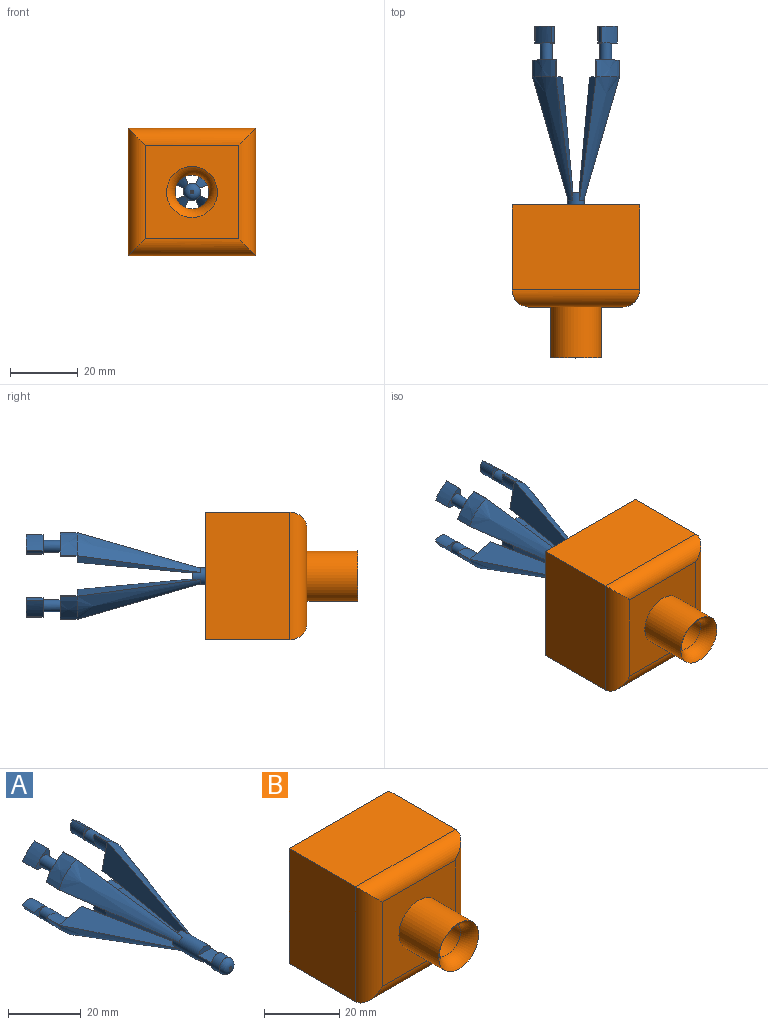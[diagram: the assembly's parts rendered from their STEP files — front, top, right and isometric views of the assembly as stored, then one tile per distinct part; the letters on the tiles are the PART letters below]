
ASSEMBLY  parts=2 mates=1
PART A: 81 faces, bbox 25.6x69x25.6 mm
  f0: plane 4.85x1.9mm, normal (0,-1,0), area 6.8mm2, adj f69,f74
  f1: bspline ~36.31x11.75mm, area 221.5mm2, adj f2,f3,f9,f69
  f2: bspline ~36.31x12.1mm, area 190.1mm2, adj f1,f3,f5,f6,f69,f71
  f3: bspline ~36.27x12.11mm, area 190.1mm2, adj f1,f2,f5,f8,f69,f71
  f4: plane 5.32x4.19mm, normal (0,1,0), area 7mm2, adj f7,f8,f9,f11
  f5: plane 8.66x8.66mm, normal (0,1,0), area 18.3mm2, adj f2,f3,f7
  f6: plane 5x0.12mm, normal (0.98,0,0.22), area 0.6mm2, adj f2,f7,f9,f10
  f7: cylinder r=5.66mm len=6.84mm, axis (0,-1,0), area 56.3mm2, adj f4,f5,f6,f8,f10
  f8: plane 5x0.12mm, normal (-0.22,0,-0.98), area 0.6mm2, adj f3,f4,f7,f9
  f9: extruded ~6.82x6.81mm, area 49.2mm2, adj f1,f4,f6,f8,f10
  f10: plane 5.31x4.18mm, normal (0,1,0), area 7mm2, adj f6,f7,f9,f11
  f11: cylinder r=1.77mm len=5mm, axis (0,-1,0), area 55.5mm2, adj f4,f10,f12,f13,f14,f15
  f12: plane 0.53x0.42mm, normal (0,1,0), area 0mm2, adj f11,f16
  f13: plane 4.04x3.28mm, normal (0,-1,0), area 3.4mm2, adj f11,f15,f16
  f14: plane 4.54x3.52mm, normal (0,-1,0), area 4.5mm2, adj f11,f15,f16
  f15: cylinder r=14.1mm len=5mm, axis (0,-1,0), area 33.3mm2, adj f11,f13,f14,f16,f17
  f16: cylinder r=3.3mm len=5.55mm, axis (0,-1,0), area 50.2mm2, adj f12,f13,f14,f15,f17
  f17: plane 5.55x5.49mm, normal (0,1,0), area 17.8mm2, adj f15,f16
  f18: bspline ~36.31x11.75mm, area 221.5mm2, adj f19,f20,f26,f69
  f19: bspline ~36.31x12.1mm, area 190.1mm2, adj f18,f20,f22,f23,f69,f71
  f20: bspline ~36.27x12.11mm, area 190.1mm2, adj f18,f19,f22,f25,f69,f71
  f21: plane 5.32x4.19mm, normal (0,1,0), area 7mm2, adj f24,f25,f26,f28
  f22: plane 8.66x8.66mm, normal (0,1,0), area 18.3mm2, adj f19,f20,f24
  f23: plane 5x0.12mm, normal (-0.22,0,0.98), area 0.6mm2, adj f19,f24,f26,f27
  f24: cylinder r=5.66mm len=6.84mm, axis (0,-1,0), area 56.3mm2, adj f21,f22,f23,f25,f27
  f25: plane 5x0.12mm, normal (0.98,0,-0.22), area 0.6mm2, adj f20,f21,f24,f26
  f26: extruded ~6.82x6.81mm, area 49.2mm2, adj f18,f21,f23,f25,f27
  f27: plane 5.31x4.18mm, normal (0,1,0), area 7mm2, adj f23,f24,f26,f28
  f28: cylinder r=1.77mm len=5mm, axis (0,-1,0), area 55.5mm2, adj f21,f27,f29,f30,f31,f32
  f29: plane 0.53x0.42mm, normal (0,1,0), area 0mm2, adj f28,f33
  f30: plane 4.04x3.28mm, normal (0,-1,0), area 3.4mm2, adj f28,f32,f33
  f31: plane 4.54x3.52mm, normal (0,-1,0), area 4.5mm2, adj f28,f32,f33
  f32: cylinder r=14.1mm len=5mm, axis (0,-1,0), area 33.3mm2, adj f28,f30,f31,f33,f34
  f33: cylinder r=3.3mm len=5.55mm, axis (0,-1,0), area 50.2mm2, adj f29,f30,f31,f32,f34
  f34: plane 5.55x5.49mm, normal (0,1,0), area 17.8mm2, adj f32,f33
  f35: bspline ~36.31x11.75mm, area 221.5mm2, adj f36,f37,f43,f69
  f36: bspline ~36.31x12.1mm, area 190.1mm2, adj f35,f37,f39,f40,f69,f71
  f37: bspline ~36.27x12.11mm, area 190.1mm2, adj f35,f36,f39,f42,f69,f71
  f38: plane 5.32x4.19mm, normal (0,1,0), area 7mm2, adj f41,f42,f43,f45
  f39: plane 8.66x8.66mm, normal (0,1,0), area 18.3mm2, adj f36,f37,f41
  f40: plane 5x0.12mm, normal (-0.98,0,-0.22), area 0.6mm2, adj f36,f41,f43,f44
  f41: cylinder r=5.66mm len=6.84mm, axis (0,-1,0), area 56.3mm2, adj f38,f39,f40,f42,f44
  f42: plane 5x0.12mm, normal (0.22,0,0.98), area 0.6mm2, adj f37,f38,f41,f43
  f43: extruded ~6.82x6.81mm, area 49.2mm2, adj f35,f38,f40,f42,f44
  f44: plane 5.31x4.18mm, normal (0,1,0), area 7mm2, adj f40,f41,f43,f45
  f45: cylinder r=1.77mm len=5mm, axis (0,-1,0), area 55.5mm2, adj f38,f44,f46,f47,f48,f49
  f46: plane 0.53x0.42mm, normal (0,1,0), area 0mm2, adj f45,f50
  f47: plane 4.04x3.28mm, normal (0,-1,0), area 3.4mm2, adj f45,f49,f50
  f48: plane 4.54x3.52mm, normal (0,-1,0), area 4.5mm2, adj f45,f49,f50
  f49: cylinder r=14.1mm len=5mm, axis (0,-1,0), area 33.3mm2, adj f45,f47,f48,f50,f51
  f50: cylinder r=3.3mm len=5.55mm, axis (0,-1,0), area 50.2mm2, adj f46,f47,f48,f49,f51
  f51: plane 5.55x5.49mm, normal (0,1,0), area 17.8mm2, adj f49,f50
  f52: bspline ~36.31x11.75mm, area 221.5mm2, adj f53,f54,f60,f69
  f53: bspline ~36.31x12.1mm, area 190.1mm2, adj f52,f54,f56,f57,f69,f71
  f54: bspline ~36.27x12.11mm, area 190.1mm2, adj f52,f53,f56,f59,f70,f71
  f55: plane 5.32x4.19mm, normal (0,1,0), area 7mm2, adj f58,f59,f60,f62
  f56: plane 8.66x8.66mm, normal (0,1,0), area 18.3mm2, adj f53,f54,f58
  f57: plane 5x0.12mm, normal (0.22,0,-0.98), area 0.6mm2, adj f53,f58,f60,f61
  f58: cylinder r=5.66mm len=6.84mm, axis (0,-1,0), area 56.3mm2, adj f55,f56,f57,f59,f61
  f59: plane 5x0.12mm, normal (-0.98,0,0.22), area 0.6mm2, adj f54,f55,f58,f60
  f60: extruded ~6.82x6.81mm, area 49.2mm2, adj f52,f55,f57,f59,f61
  f61: plane 5.31x4.18mm, normal (0,1,0), area 7mm2, adj f57,f58,f60,f62
  f62: cylinder r=1.77mm len=5mm, axis (0,-1,0), area 55.5mm2, adj f55,f61,f63,f64,f65,f66
  f63: plane 0.53x0.42mm, normal (0,1,0), area 0mm2, adj f62,f67
  f64: plane 4.04x3.28mm, normal (0,-1,0), area 3.4mm2, adj f62,f66,f67
  f65: plane 4.54x3.52mm, normal (0,-1,0), area 4.5mm2, adj f62,f66,f67
  f66: cylinder r=14.1mm len=5mm, axis (0,-1,0), area 33.3mm2, adj f62,f64,f65,f67,f68
  f67: cylinder r=3.3mm len=5.55mm, axis (0,-1,0), area 50.2mm2, adj f63,f64,f65,f66,f68
  f68: plane 5.55x5.49mm, normal (0,1,0), area 17.8mm2, adj f66,f67
  f69: cylinder r=2.5mm len=18mm, axis (0,1,0), area 201.2mm2, adj f0,f1,f2,f3,f18,f19,f20,f35
  f70: cylinder r=2.5mm len=2.27mm, axis (0,1,0), area 0.2mm2, adj f54,f69,f71
  f71: plane 5x5mm, normal (0,1,0), area 15.9mm2, adj f2,f3,f19,f20,f36,f37,f53,f54
  f72: plane 4.85x1.9mm, normal (0,-1,0), area 6.8mm2, adj f69,f73
  f73: plane 5x4.85mm, normal (0,0,1), area 24.3mm2, adj f69,f72,f77
  f74: plane 5x4.85mm, normal (0,0,-1), area 24.3mm2, adj f0,f69,f75
  f75: plane 4.85x1.9mm, normal (0,1,0), area 6.8mm2, adj f69,f74
  f76: plane 1x1mm, normal (0,-1,0), area 0.8mm2, adj f79,f80
  f77: plane 4.85x1.9mm, normal (0,1,0), area 6.8mm2, adj f69,f73
  f78: plane 0.1x0.1mm, normal (0,-1,0), area 0mm2, adj f79
  f79: cylinder r=0.05mm len=9mm, axis (0,1,0), area 2.8mm2, adj f76,f78
  f80: torus R=0.5mm, axis (0,-1,0), area 35mm2, adj f69,f76
PART B: 19 faces, bbox 37.5x45.7x37.5 mm
  f0: cylinder r=5mm len=15.67mm, axis (0,-1,0), area 492.3mm2, adj f13,f14
  f1: plane 37.5x37.5mm, normal (0,1,0), area 781.2mm2, adj f2,f3,f4,f5,f7,f8,f9,f10
  f2: plane 37.5x25mm, normal (0,0,-1), area 937.5mm2, adj f1,f3,f5,f15
  f3: plane 37.5x25mm, normal (1,0,0), area 937.5mm2, adj f1,f2,f4,f16
  f4: plane 37.5x25mm, normal (0,0,1), area 937.5mm2, adj f1,f3,f5,f18
  f5: plane 37.5x25mm, normal (-1,0,0), area 937.5mm2, adj f1,f2,f4,f17
  f6: plane 27.5x27.5mm, normal (0,-1,0), area 579.5mm2, adj f12,f15,f16,f17,f18
  f7: plane 25x20mm, normal (1,0,0), area 500mm2, adj f1,f8,f10,f11
  f8: plane 25x20mm, normal (0,0,-1), area 500mm2, adj f1,f7,f9,f11
  f9: plane 25x20mm, normal (-1,0,0), area 500mm2, adj f1,f8,f10,f11
  f10: plane 25x20mm, normal (0,0,1), area 500mm2, adj f1,f7,f9,f11
  f11: plane 25x25mm, normal (0,1,0), area 310.8mm2, adj f7,f8,f9,f10,f14
  f12: cylinder r=7.5mm len=15mm, axis (0,1,0), area 706.9mm2, adj f6,f13
  f13: torus R=10mm, axis (0,-1,0), area 193mm2, adj f0,f12
  f14: torus R=10mm, axis (0,1,0), area 336.4mm2, adj f0,f11
  f15: cylinder r=5mm len=37.5mm, axis (1,0,0), area 266mm2, adj f2,f6,f16,f17
  f16: cylinder r=5mm len=37.5mm, axis (0,0,1), area 266mm2, adj f3,f6,f15,f18
  f17: cylinder r=5mm len=37.5mm, axis (0,0,-1), area 266mm2, adj f5,f6,f15,f18
  f18: cylinder r=5mm len=37.5mm, axis (-1,0,0), area 266mm2, adj f4,f6,f16,f17
PLACE A t=(103.62,62.79,-3.14)mm
PLACE B t=(52.15,-0.9,-34.6)mm
MATE slider A.f69 <-> B.f0  axis (0,-1,0) through (103.62,12.79,-3.14)mm
